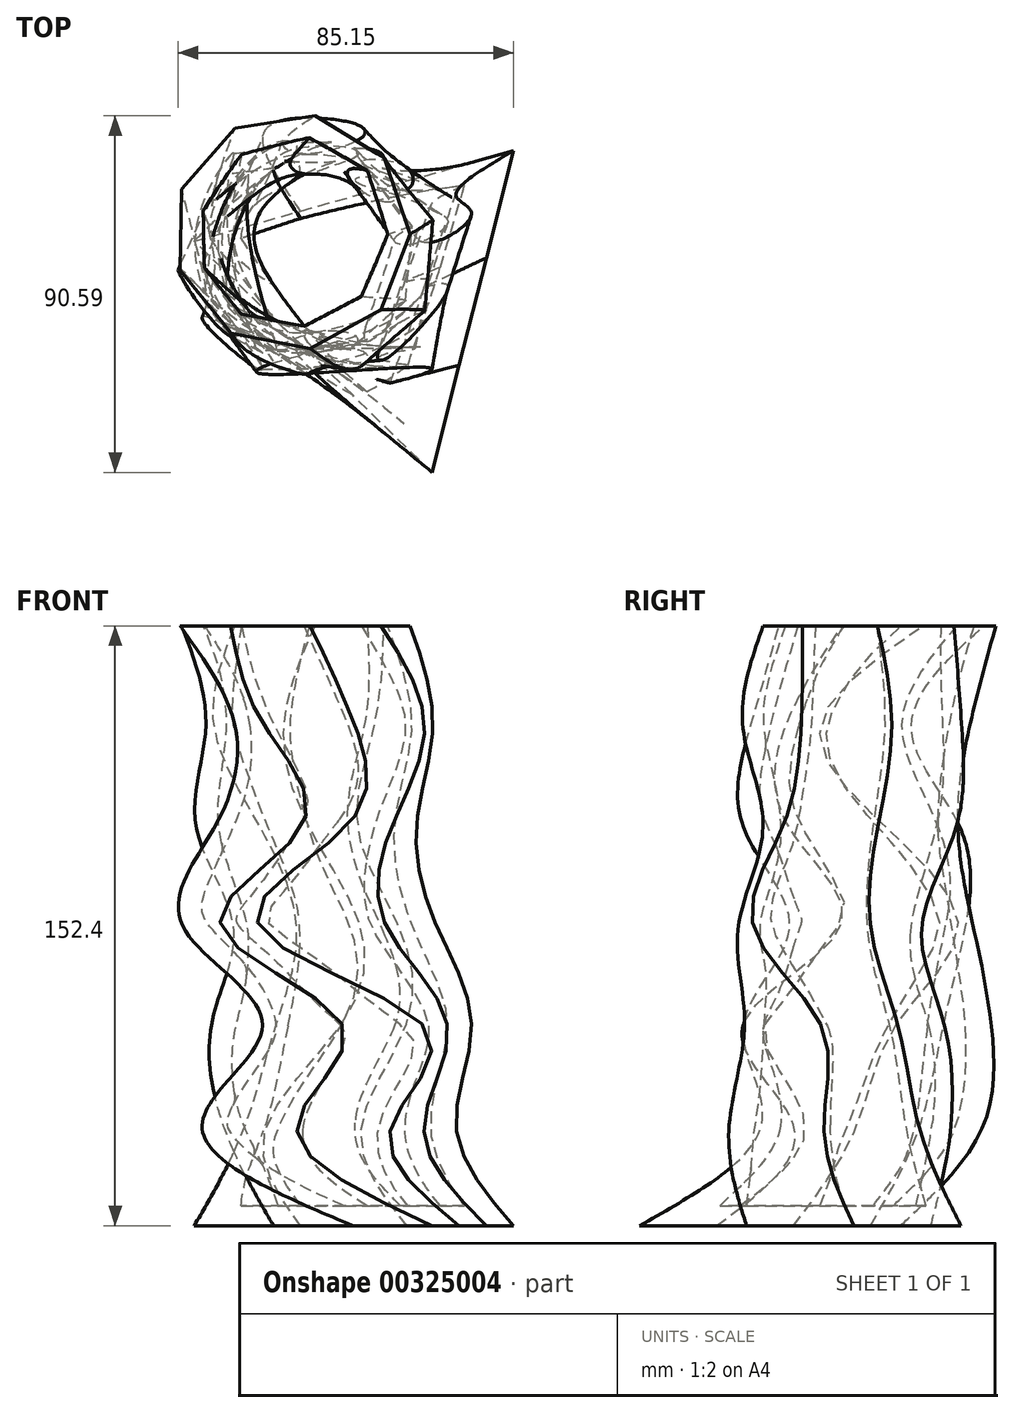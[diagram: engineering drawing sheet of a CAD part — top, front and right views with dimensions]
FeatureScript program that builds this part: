
annotation { "Feature Type Name" : "Feature", "Feature Type Description" : "" }
export const myFeature = defineFeature(function(context is Context, id is Id, definition is map)
    precondition{}
    {
        {
            var Q0;
            Q0=qCreatedBy(makeId("Top.planeOp"),FACE);
            cPlane(context, id + "F0", {"entities" : qUnion([Q0]), "cplaneType" : CPlaneType.OFFSET, "offset" : 25.4 * mm, "width" : 152.4 * mm, "height" : 152.4 * mm});
        }
        {
            var Q0;
            Q0=qCreatedBy(id+"F0.planeOp",FACE);
            cPlane(context, id + "F1", {"entities" : qUnion([Q0]), "cplaneType" : CPlaneType.OFFSET, "offset" : 25.4 * mm, "width" : 152.4 * mm, "height" : 152.4 * mm});
        }
        {
            var Q0;
            Q0=qCreatedBy(id+"F1.planeOp",FACE);
            cPlane(context, id + "F2", {"entities" : qUnion([Q0]), "cplaneType" : CPlaneType.OFFSET, "offset" : 25.4 * mm, "width" : 152.4 * mm, "height" : 152.4 * mm});
        }
        {
            var Q0;
            Q0=qCreatedBy(id+"F2.planeOp",FACE);
            cPlane(context, id + "F3", {"entities" : qUnion([Q0]), "cplaneType" : CPlaneType.OFFSET, "offset" : 25.4 * mm, "width" : 152.4 * mm, "height" : 152.4 * mm});
        }
        {
            var Q0;
            Q0=qCreatedBy(id+"F3.planeOp",FACE);
            cPlane(context, id + "F4", {"entities" : qUnion([Q0]), "cplaneType" : CPlaneType.OFFSET, "offset" : 25.4 * mm, "width" : 152.4 * mm, "height" : 152.4 * mm});
        }
        {
            var Q0;
            Q0=qCreatedBy(id+"F4.planeOp",FACE);
            cPlane(context, id + "F5", {"entities" : qUnion([Q0]), "cplaneType" : CPlaneType.OFFSET, "offset" : 25.4 * mm, "width" : 152.4 * mm, "height" : 152.4 * mm});
        }
        {
            var Q0;
            Q0=qCreatedBy(makeId("Top.planeOp"),FACE);
            var sketch = newSketch(context, id + "F6", { "sketchPlane" : qUnion([Q0])});
            skPoint(sketch, "E0.0.midPoint", {"position": v(5.32, 0) * mm});
            skPoint(sketch, "E1.orphan", {"position": v(14.42, 10.47) * mm});
            skPoint(sketch, "E0.1.start.orphan", {"position": v(-3.78, -10.47) * mm});
            skCircle(sketch, "E2.cCircle", {"center": v(-17.15, 3.02) * mm, "radius": 24.33 * mm, "construction": true});
            skLineSegment(sketch, "E2.0", {"start": v(16.76, 37.91) * mm, "end": v(-3.89, -43.8) * mm});
            skLineSegment(sketch, "E2.1", {"start": v(-3.89, -43.8) * mm, "end": v(-64.33, 14.94) * mm});
            skLineSegment(sketch, "E2.2", {"start": v(-64.33, 14.94) * mm, "end": v(16.76, 37.91) * mm});
            skPoint(sketch, "E2.0.midPoint", {"position": v(6.43, -2.94) * mm});
            skSolve(sketch);
        }
        {
            var Q0;
            Q0=qCreatedBy(id+"F0.planeOp",FACE);
            var sketch = newSketch(context, id + "F7", { "sketchPlane" : qUnion([Q0])});
            skCircle(sketch, "E3.cCircle", {"center": v(-30.06, 11.28) * mm, "radius": 25.44 * mm, "construction": true});
            skLineSegment(sketch, "E3.0", {"start": v(2.21, 27.17) * mm, "end": v(-14.17, -21) * mm});
            skLineSegment(sketch, "E3.1", {"start": v(-14.17, -21) * mm, "end": v(-62.34, -4.61) * mm});
            skLineSegment(sketch, "E3.2", {"start": v(-62.34, -4.61) * mm, "end": v(-45.95, 43.56) * mm});
            skLineSegment(sketch, "E3.3", {"start": v(-45.95, 43.56) * mm, "end": v(2.21, 27.17) * mm});
            skPoint(sketch, "E3.0.midPoint", {"position": v(-5.98, 3.08) * mm});
            skSolve(sketch);
        }
        {
            var Q0;
            Q0=qCreatedBy(id+"F1.planeOp",FACE);
            var sketch = newSketch(context, id + "F8", { "sketchPlane" : qUnion([Q0])});
            skCircle(sketch, "E4.cCircle", {"center": v(-26.84, 10.85) * mm, "radius": 28.13 * mm, "construction": true});
            skLineSegment(sketch, "E4.0", {"start": v(6.13, 21.9) * mm, "end": v(-6.13, -17.1) * mm});
            skLineSegment(sketch, "E4.1", {"start": v(-6.13, -17.1) * mm, "end": v(-47.01, -17.47) * mm});
            skLineSegment(sketch, "E4.2", {"start": v(-47.01, -17.47) * mm, "end": v(-60, 21.28) * mm});
            skLineSegment(sketch, "E4.3", {"start": v(-60, 21.28) * mm, "end": v(-27.16, 45.62) * mm});
            skLineSegment(sketch, "E4.4", {"start": v(-27.16, 45.62) * mm, "end": v(6.13, 21.9) * mm});
            skPoint(sketch, "E4.0.midPoint", {"position": v(0, 2.4) * mm});
            skSolve(sketch);
        }
        {
            var Q0;
            Q0=qCreatedBy(id+"F2.planeOp",FACE);
            var sketch = newSketch(context, id + "F9", { "sketchPlane" : qUnion([Q0])});
            skCircle(sketch, "E5.cCircle", {"center": v(-35.03, 11.16) * mm, "radius": 28.13 * mm, "construction": true});
            skLineSegment(sketch, "E5.0", {"start": v(-2.76, 14.9) * mm, "end": v(-15.65, -14.9) * mm});
            skLineSegment(sketch, "E5.1", {"start": v(-15.65, -14.9) * mm, "end": v(-47.92, -18.65) * mm});
            skLineSegment(sketch, "E5.2", {"start": v(-47.92, -18.65) * mm, "end": v(-67.3, 7.42) * mm});
            skLineSegment(sketch, "E5.3", {"start": v(-67.3, 7.42) * mm, "end": v(-54.4, 37.24) * mm});
            skLineSegment(sketch, "E5.4", {"start": v(-54.4, 37.24) * mm, "end": v(-22.14, 40.98) * mm});
            skLineSegment(sketch, "E5.5", {"start": v(-22.14, 40.98) * mm, "end": v(-2.76, 14.9) * mm});
            skPoint(sketch, "E5.0.midPoint", {"position": v(-9.2, 0) * mm});
            skSolve(sketch);
        }
        {
            var Q0;
            Q0=qCreatedBy(id+"F3.planeOp",FACE);
            var sketch = newSketch(context, id + "F10", { "sketchPlane" : qUnion([Q0])});
            skCircle(sketch, "E6.cCircle", {"center": v(-36.02, 11.23) * mm, "radius": 25.9 * mm, "construction": true});
            skLineSegment(sketch, "E6.0", {"start": v(-7.84, 16.85) * mm, "end": v(-14.06, -7.3) * mm});
            skLineSegment(sketch, "E6.1", {"start": v(-14.06, -7.3) * mm, "end": v(-36.82, -17.5) * mm});
            skLineSegment(sketch, "E6.2", {"start": v(-36.82, -17.5) * mm, "end": v(-58.98, -6.06) * mm});
            skLineSegment(sketch, "E6.3", {"start": v(-58.98, -6.06) * mm, "end": v(-63.86, 18.4) * mm});
            skLineSegment(sketch, "E6.4", {"start": v(-63.86, 18.4) * mm, "end": v(-47.78, 37.46) * mm});
            skLineSegment(sketch, "E6.5", {"start": v(-47.78, 37.46) * mm, "end": v(-22.84, 36.77) * mm});
            skLineSegment(sketch, "E6.6", {"start": v(-22.84, 36.77) * mm, "end": v(-7.84, 16.85) * mm});
            skPoint(sketch, "E6.0.midPoint", {"position": v(-10.95, 4.78) * mm});
            skSolve(sketch);
        }
        {
            var Q0;
            Q0=qCreatedBy(id+"F4.planeOp",FACE);
            var sketch = newSketch(context, id + "F11", { "sketchPlane" : qUnion([Q0])});
            skCircle(sketch, "E7.cCircle", {"center": v(-32.55, 11.3) * mm, "radius": 27.92 * mm, "construction": true});
            skLineSegment(sketch, "E7.0", {"start": v(-3.71, 20.34) * mm, "end": v(-5.77, -2.7) * mm});
            skLineSegment(sketch, "E7.1", {"start": v(-5.77, -2.7) * mm, "end": v(-23.51, -17.54) * mm});
            skLineSegment(sketch, "E7.2", {"start": v(-23.51, -17.54) * mm, "end": v(-46.55, -15.48) * mm});
            skLineSegment(sketch, "E7.3", {"start": v(-46.55, -15.48) * mm, "end": v(-61.38, 2.26) * mm});
            skLineSegment(sketch, "E7.4", {"start": v(-61.38, 2.26) * mm, "end": v(-59.33, 25.3) * mm});
            skLineSegment(sketch, "E7.5", {"start": v(-59.33, 25.3) * mm, "end": v(-41.58, 40.14) * mm});
            skLineSegment(sketch, "E7.6", {"start": v(-41.58, 40.14) * mm, "end": v(-18.55, 38.08) * mm});
            skLineSegment(sketch, "E7.7", {"start": v(-18.55, 38.08) * mm, "end": v(-3.71, 20.34) * mm});
            skPoint(sketch, "E7.0.midPoint", {"position": v(-4.74, 8.82) * mm});
            skSolve(sketch);
        }
        {
            var Q0;
            Q0=qCreatedBy(id+"F5.planeOp",FACE);
            var sketch = newSketch(context, id + "F12", { "sketchPlane" : qUnion([Q0])});
            skCircle(sketch, "E8.cCircle", {"center": v(-39.5, 17.33) * mm, "radius": 28.22 * mm, "construction": true});
            skLineSegment(sketch, "E8.0", {"start": v(-9.48, 16.73) * mm, "end": v(-16.89, -2.43) * mm});
            skLineSegment(sketch, "E8.1", {"start": v(-16.89, -2.43) * mm, "end": v(-34.88, -12.35) * mm});
            skLineSegment(sketch, "E8.2", {"start": v(-34.88, -12.35) * mm, "end": v(-55.03, -8.37) * mm});
            skLineSegment(sketch, "E8.3", {"start": v(-55.03, -8.37) * mm, "end": v(-67.92, 7.62) * mm});
            skLineSegment(sketch, "E8.4", {"start": v(-67.92, 7.62) * mm, "end": v(-67.5, 28.16) * mm});
            skLineSegment(sketch, "E8.5", {"start": v(-67.5, 28.16) * mm, "end": v(-54, 43.63) * mm});
            skLineSegment(sketch, "E8.6", {"start": v(-54, 43.63) * mm, "end": v(-33.7, 46.8) * mm});
            skLineSegment(sketch, "E8.7", {"start": v(-33.7, 46.8) * mm, "end": v(-16.11, 36.17) * mm});
            skLineSegment(sketch, "E8.8", {"start": v(-16.11, 36.17) * mm, "end": v(-9.48, 16.73) * mm});
            skPoint(sketch, "E8.0.midPoint", {"position": v(-13.18, 7.15) * mm});
            skSolve(sketch);
        }
        {
            var Q0;
            Q0=makeQuery(id+"F6.imprint","IMPRINT",FACE,{"disambiguationData":[TD([[makeQuery(id+"F6.imprint","IMPRINT",EDGE,{"derivedFrom":sQuery(id+"F6.wireOp",EDGE,"E2.0")}),-1.0]])]});
            var Q1;
            Q1=makeQuery(id+"F7.imprint","IMPRINT",FACE,{"disambiguationData":[TD([[makeQuery(id+"F7.imprint","IMPRINT",EDGE,{"derivedFrom":sQuery(id+"F7.wireOp",EDGE,"E3.0")}),-1.0]])]});
            var Q2;
            Q2=makeQuery(id+"F8.imprint","IMPRINT",FACE,{"disambiguationData":[TD([[makeQuery(id+"F8.imprint","IMPRINT",EDGE,{"derivedFrom":sQuery(id+"F8.wireOp",EDGE,"E4.0")}),-1.0]])]});
            var Q3;
            Q3=makeQuery(id+"F9.imprint","IMPRINT",FACE,{"disambiguationData":[TD([[makeQuery(id+"F9.imprint","IMPRINT",EDGE,{"derivedFrom":sQuery(id+"F9.wireOp",EDGE,"E5.0")}),-1.0]])]});
            var Q4;
            Q4=makeQuery(id+"F10.imprint","IMPRINT",FACE,{"disambiguationData":[TD([[makeQuery(id+"F10.imprint","IMPRINT",EDGE,{"derivedFrom":sQuery(id+"F10.wireOp",EDGE,"E6.0")}),-1.0]])]});
            var Q5;
            Q5=makeQuery(id+"F11.imprint","IMPRINT",FACE,{"disambiguationData":[TD([[makeQuery(id+"F11.imprint","IMPRINT",EDGE,{"derivedFrom":sQuery(id+"F11.wireOp",EDGE,"E7.0")}),-1.0]])]});
            var Q6;
            Q6=makeQuery(id+"F12.imprint","IMPRINT",FACE,{"disambiguationData":[TD([[makeQuery(id+"F12.imprint","IMPRINT",EDGE,{"derivedFrom":sQuery(id+"F12.wireOp",EDGE,"E8.0")}),-1.0]])]});
            loft(context, id + "F13", {"sheetProfilesArray" : [{ "sheetProfileEntities" : qUnion([Q0]) }, { "sheetProfileEntities" : qUnion([Q1]) }, { "sheetProfileEntities" : qUnion([Q2]) }, { "sheetProfileEntities" : qUnion([Q3]) }, { "sheetProfileEntities" : qUnion([Q4]) }, { "sheetProfileEntities" : qUnion([Q5]) }, { "sheetProfileEntities" : qUnion([Q6]) }]});
        }
        {
            var Q0;
            Q0=makeQuery(id+"F13.opLoft","CAP_FACE",FACE,{"disambiguationData":[OSD([makeQuery(id+"F12.imprint","IMPRINT",FACE,{"disambiguationData":[TD([[makeQuery(id+"F12.imprint","IMPRINT",EDGE,{"derivedFrom":sQuery(id+"F12.wireOp",EDGE,"E8.0")}),-1.0]])]})])],"isStart":true});
            shell(context, id + "F14", {"entities" : qUnion([Q0]), "thickness" : 5.08 * mm});
        }
    });
